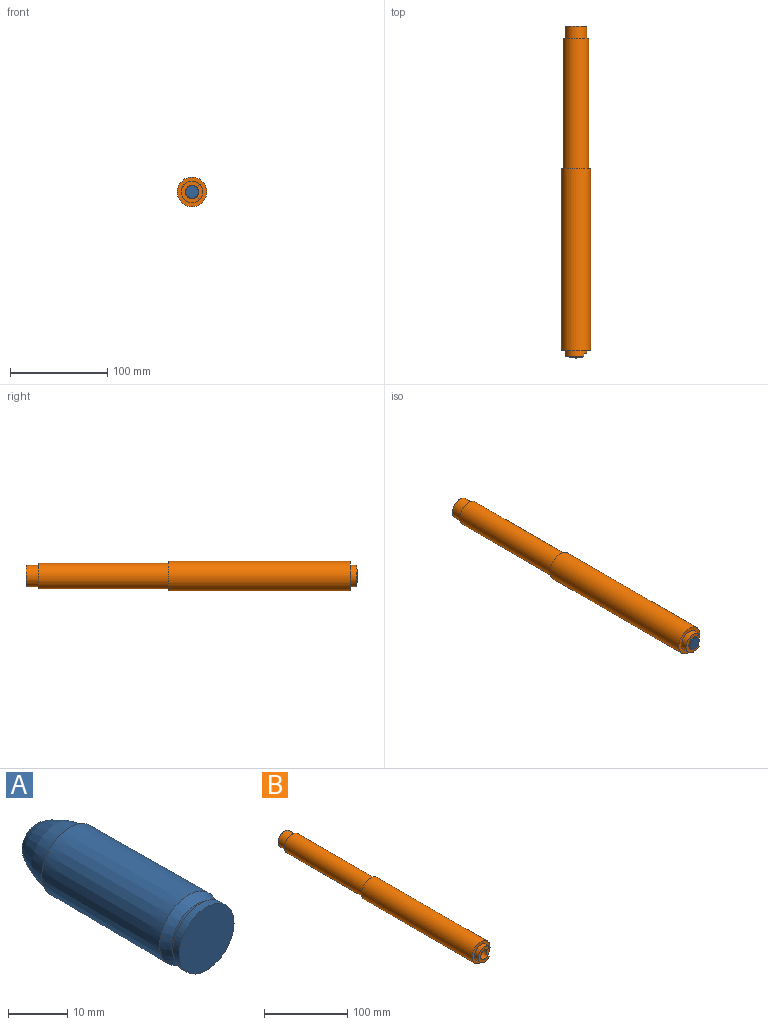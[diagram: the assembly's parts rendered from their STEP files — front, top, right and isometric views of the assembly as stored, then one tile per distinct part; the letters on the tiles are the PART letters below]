
ASSEMBLY  parts=2 mates=1
PART A: 9 faces, bbox 13.8x40.5x13.8 mm
  f0: plane 13.44x13.44mm, normal (0,1,0), area 14.1mm2, adj f1,f8
  f1: cone r=6.9mm half-angle=0.4deg, axis (0,-1,0), area 1211.5mm2, adj f0,f2
  f2: cone r=5.84mm half-angle=30deg, axis (0,1,0), area 84.8mm2, adj f1,f3
  f3: cylinder r=5.84mm len=11.68mm, axis (0,1,0), area 35.4mm2, adj f2,f4
  f4: plane 13.08x13.08mm, normal (0,1,0), area 27.2mm2, adj f3,f5
  f5: cylinder r=6.54mm len=13.08mm, axis (0,1,0), area 62.6mm2, adj f4,f6
  f6: plane 13.08x13.08mm, normal (0,-1,0), area 134.4mm2, adj f5
  f7: plane 7.19x7.19mm, normal (0,1,0), area 40.6mm2, adj f8
  f8: revolved ~12.75x12.75mm, area 284.9mm2, adj f0,f7
PART B: 16 faces, bbox 30.5x339.7x30.5 mm
  f0: cone r=6.74mm half-angle=0.3deg, axis (0,-1,0), area 1381.8mm2, adj f2,f12,f13,f14,f15
  f1: cylinder r=11.11mm len=22.23mm, axis (0,1,0), area 387.9mm2, adj f11,f12,f13,f14,f15
  f2: plane 13.49x13.49mm, normal (0,-1,0), area 14.7mm2, adj f0,f3
  f3: cone r=6.2mm half-angle=2.8deg, axis (0,-1,0), area 154.8mm2, adj f2,f4
  f4: cylinder r=6.2mm len=302.87mm, axis (0,1,0), area 11793.9mm2, adj f3,f5
  f5: plane 22.23x22.23mm, normal (0,1,0), area 267.3mm2, adj f4,f6
  f6: cylinder r=11.11mm len=22.23mm, axis (0,1,0), area 886.7mm2, adj f5,f7
  f7: plane 26.35x26.35mm, normal (0,1,0), area 157.5mm2, adj f6,f8
  f8: cylinder r=13.18mm len=133.35mm, axis (0,1,0), area 11039.9mm2, adj f7,f9
  f9: plane 30.48x30.48mm, normal (0,1,0), area 184.2mm2, adj f8,f10
  f10: cylinder r=15.24mm len=187.33mm, axis (0,1,0), area 17937.4mm2, adj f9,f11
  f11: plane 30.48x30.48mm, normal (0,-1,0), area 341.7mm2, adj f1,f10
  f12: plane 22.23x18.97mm, normal (0,-1,0), area 177.4mm2, adj f0,f1,f14,f15
  f13: plane 15.72x6.22mm, normal (0,-1,0), area 59.3mm2, adj f0,f1,f14,f15
  f14: plane 3.18x2.96mm, normal (0.71,0,-0.71), area 13.3mm2, adj f0,f1,f12,f13
  f15: plane 3.18x2.96mm, normal (0.71,0,0.71), area 13.3mm2, adj f0,f1,f12,f13
PLACE A t=(1.15,-10.73,13.28)mm
PLACE B t=(1.15,-9.21,13.28)mm
MATE fastened B.f0 <-> A.f1  axis (0,-1,0) through (1.15,-9.21,13.28)mm
